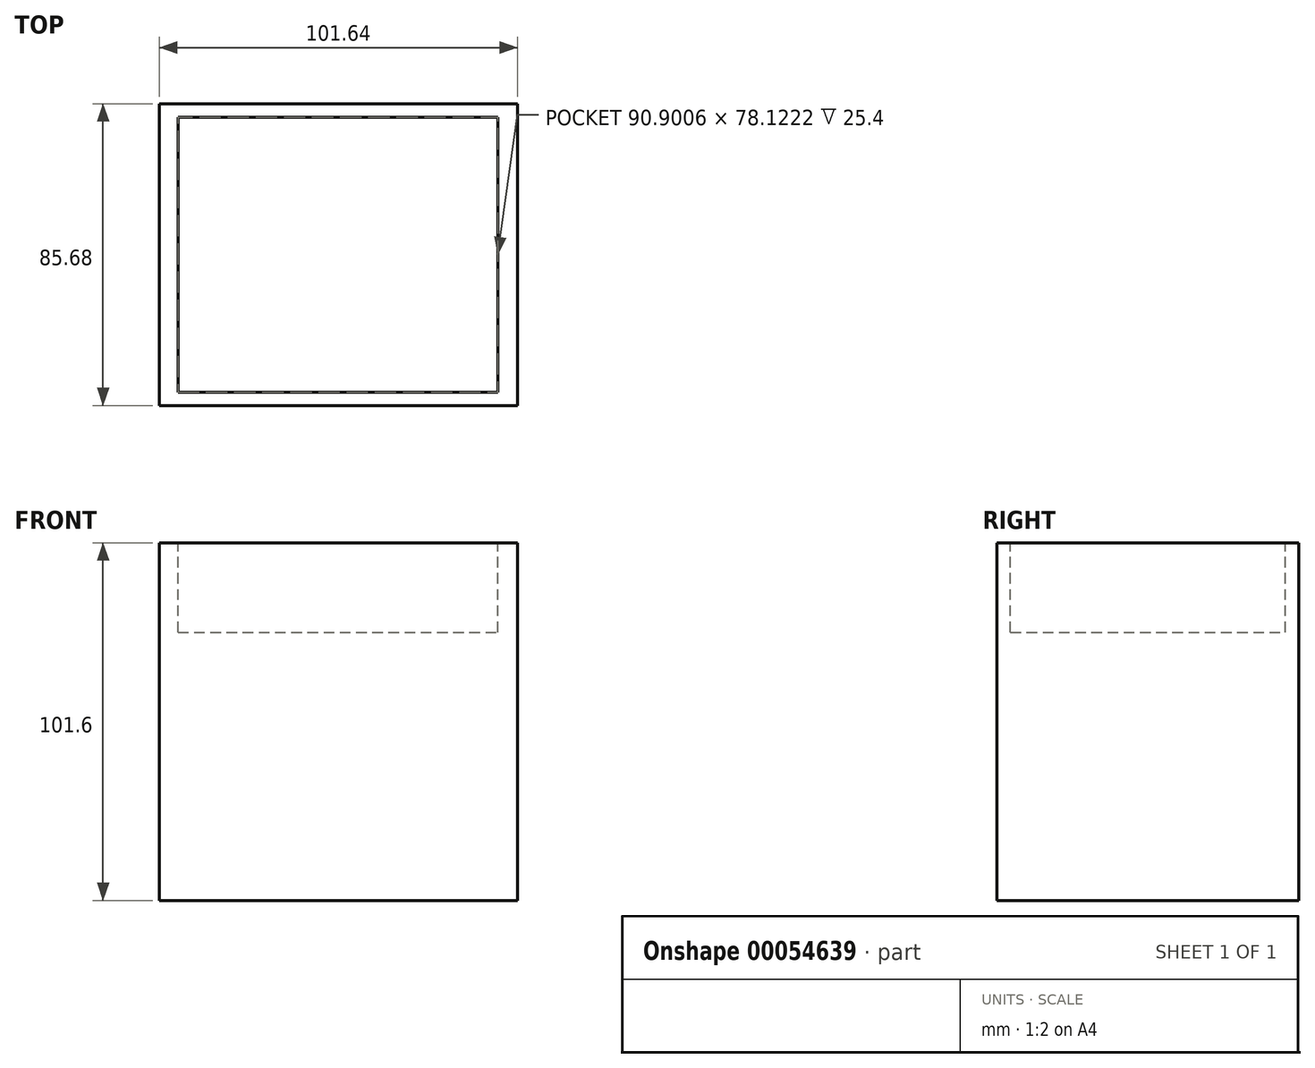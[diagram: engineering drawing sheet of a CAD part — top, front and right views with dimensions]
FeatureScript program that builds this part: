
annotation { "Feature Type Name" : "Feature", "Feature Type Description" : "" }
export const myFeature = defineFeature(function(context is Context, id is Id, definition is map)
    precondition{}
    {
        {
            var Q0;
            Q0=qCreatedBy(makeId("Top.planeOp"),FACE);
            var sketch = newSketch(context, id + "F0", { "sketchPlane" : qUnion([Q0])});
            skLineSegment(sketch, "E0.rect.bottom", {"start": v(-50.82, -42.84) * mm, "end": v(50.82, -42.84) * mm});
            skLineSegment(sketch, "E0.rect.top", {"start": v(-50.82, 42.84) * mm, "end": v(50.82, 42.84) * mm});
            skLineSegment(sketch, "E0.rect.left", {"start": v(-50.82, -42.84) * mm, "end": v(-50.82, 42.84) * mm});
            skLineSegment(sketch, "E0.rect.right", {"start": v(50.82, -42.84) * mm, "end": v(50.82, 42.84) * mm});
            skPoint(sketch, "E0.rect.middle", {"position": v(0, 0) * mm});
            skSolve(sketch);
        }
        {
            var Q0;
            Q0=makeQuery(id+"F0.imprint","IMPRINT",FACE,{"disambiguationData":[TD([[makeQuery(id+"F0.imprint","IMPRINT",EDGE,{"derivedFrom":sQuery(id+"F0.wireOp",EDGE,"E0.rect.bottom")}),1.0]])]});
            extrude(context, id + "F1", {"entities" : qUnion([Q0]), "depth" : 101.6 * mm});
        }
        {
            var Q0;
            Q0=makeQuery(id+"F1.opExtrude","CAP_FACE",FACE,{"disambiguationData":[OSD([sQuery(id+"F0.wireOp",EDGE,"E0.rect.bottom"),sQuery(id+"F0.wireOp",EDGE,"E0.rect.top"),sQuery(id+"F0.wireOp",EDGE,"E0.rect.left"),sQuery(id+"F0.wireOp",EDGE,"E0.rect.right")])],"isStart":false});
            var sketch = newSketch(context, id + "F2", { "sketchPlane" : qUnion([Q0])});
            skLineSegment(sketch, "E1.bottom", {"start": v(-45.6, -39.06) * mm, "end": v(45.3, -39.06) * mm});
            skLineSegment(sketch, "E1.top", {"start": v(-45.6, 39.06) * mm, "end": v(45.3, 39.06) * mm});
            skLineSegment(sketch, "E1.left", {"start": v(-45.6, -39.06) * mm, "end": v(-45.6, 39.06) * mm});
            skLineSegment(sketch, "E1.right", {"start": v(45.3, -39.06) * mm, "end": v(45.3, 39.06) * mm});
            skSolve(sketch);
        }
        {
            var Q0;
            Q0=makeQuery(id+"F2.imprint","IMPRINT",FACE,{"disambiguationData":[TD([[makeQuery(id+"F2.imprint","IMPRINT",EDGE,{"derivedFrom":sQuery(id+"F2.wireOp",EDGE,"E1.bottom")}),1.0]])]});
            extrude(context, id + "F3", {"entities" : qUnion([Q0]), "operationType" : NewBodyOperationType.REMOVE, "oppositeDirection" : true, "depth" : 25.4 * mm});
        }
    });
